# Revit family: Woodfold-Accordion-Door-Family-Series-740-Double
name_source: partatom
category: Doors
units: mm (PartAtom-declared; Revit-internal decimal feet)

## family parameters
Always vertical = Yes
Cut with Voids When Loaded = No
Host = Wall
Room Calculation Point = No
Shared = No

## types (4) — shared parameters
Description = Alumifold security door
Frame Projection Ext. = 0' - 1"
Frame Projection Int. = 0' - 1"
Frame Visibility = Yes
Frame Width = 0' - 3"
Function = Interior
Height = 8' - 0"
Lead Post = Metal - Aluminum
Manufacturer = Woodfold Mfg., Inc.
Model = 740
Panel Connectors = Rigid Vinyl with steel rods
Panel Material = Woodfold - Aluminum - Clear
Stack Dimension = 1' - 3 1/2"
Track Material = Metal - Aluminum
Type Comments = Width: No limitation.  Height:Clear up to 10'-1", Braonze and Gold up to 8'-1"
Wall Closure = By host
Width = 8' - 0"

## per-type parameters (varying)
| type | Hardware Type | Recessed Track | Surface Track |
| 8'-0" x 8'-0" Surface Mounted w/Keylock | Keylock two-sides | No | Yes |
| 8'-0" x 8'-0" Surface Mounted w/Deadlatch | Deadlatch with Thumbturn Two-sides | No | Yes |
| 8'-0" x 8'-0" Recessed Track w/Deadlatch | Deadlatch with Thumbturn Two-sides | Yes | No |
| 8'-0" x 8'-0" Recessed Track w/Keylock | Keylock two-sides | Yes | No |

## geometry (parser evidence)
native form markers: Sweep x20
no freeform markers — native parametric forms only
